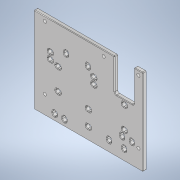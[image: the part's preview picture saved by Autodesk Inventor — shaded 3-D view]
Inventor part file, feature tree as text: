
AUTODESK INVENTOR PART (.ipt)
format: ipt  version: 2021 (Build 250183000, 183)  size: 669,696 bytes
history: native  units: mm
features: sketch x8, extrude x7, fillet x4, chamfer x1, projected_geometry x1
ambient origin geometry x8: Origin, YZ Plane, XZ Plane, XY Plane, X Axis, Y Axis, Z Axis, Center Point
bodies: Solid1 (feature_tree)
feature tree (21):
  extrude  "Extrusion1"  Depth=79.0mm
  extrude  "Extrusion2"  Depth=3.0mm
  fillet  "Fillet1"  Radius=3.0mm
  extrude  "Extrusion3"  Depth=4.0mm
  extrude  "Extrusion4"  Depth=4.0mm
  extrude  "Extrusion5"  Depth=2.0mm TaperAngle=0.0deg
  extrude  "Extrusion6"  Depth=4.0mm
  fillet  "Fillet2"  Radius=4.0mm
  sketch  "Sketch7"  dims[d18=4.0mm d19=4.0mm]
  fillet  "Fillet3"  Radius=4.0mm
  fillet  "Fillet4"  Radius=4.0mm
  extrude  "Extrusion7"  Depth=4.0mm
  chamfer  "Chamfer1"  Distance=4.0mm
  sketch  "Sketch1"  dims[d0=100.0mm d1=79.0mm]
  sketch  "Sketch2"  dims[d2=3.0mm d3=0.0mm d4=3.0mm d5=3.0mm]
  sketch  "Sketch3"  dims[d6=86.0mm d7=4.0mm]
  sketch  "Sketch4"  dims[d8=4.0mm d9=4.0mm]
  sketch  "Sketch5"  dims[d10=33.0mm d11=2.0mm d12=0.0mm]
  sketch  "Sketch6"  dims[d13=0.6mm d14=4.0mm d15=4.0mm d16=4.0mm d17=4.0mm]
  projected_geometry  "Projected Loop1"
  sketch  "Sketch8"  dims[d20=4.0mm d21=4.0mm d23=4.0mm d24=5.0mm d25=5.0mm d26=5.0mm d27=5.0mm d29=5.0mm d30=5.0mm d31=5.0mm d32=5.0mm d33=5.0mm d34=0.0mm d35=20.0mm d36=20.0mm d37=14.0mm d38=14.0mm d40=17.0mm d41=10.0mm d42=25.0mm d43=50.0mm d44=34.0mm d45=4.0mm d46=5.0mm d47=20.0mm d48=0.0mm d49=0.0mm d50=17.0mm d51=0.0mm d52=0.0mm d54=4.0mm d55=5.0mm d56=4.0mm d57=5.0mm d60=4.0mm d61=5.0mm d62=2.0mm d63=5.0mm d64=0.0mm d65=5.0mm d66=19.0mm d67=6.0mm d72=4.0mm d73=5.0mm d74=4.0mm d75=5.0mm d76=0.0mm d77=5.0mm d78=2.0mm d79=5.0mm d80=2.0mm d81=5.0mm d82=10.022273mm d83=2.022273mm d84=4.0mm d85=0.0mm d86=0.0mm d87=5.0mm d88=4.0mm d89=4.0mm d90=4.0mm d91=5.0mm d92=5.0mm d93=6.0mm d98=3.5mm d102=26.0mm d103=15.0mm d105=4.0mm d106=4.0mm d107=5.0mm d108=5.0mm d109=6.0mm d116=2.0mm d117=5.0mm d121=0.0mm d122=45.0mm d123=0.0mm d124=0.0mm d125=20.0mm d126=29.5mm d127=30.0mm d128=8.0mm d129=18.0mm d130=0.0mm d131=0.0mm d132=0.6mm d133=1.75mm d134=1.75mm d135=1.75mm d136=3.0mm d137=5.0mm d138=10.0mm d139=10.0mm d140=0.0mm d141=0.5mm d142=2.0mm d143=45.0deg]
